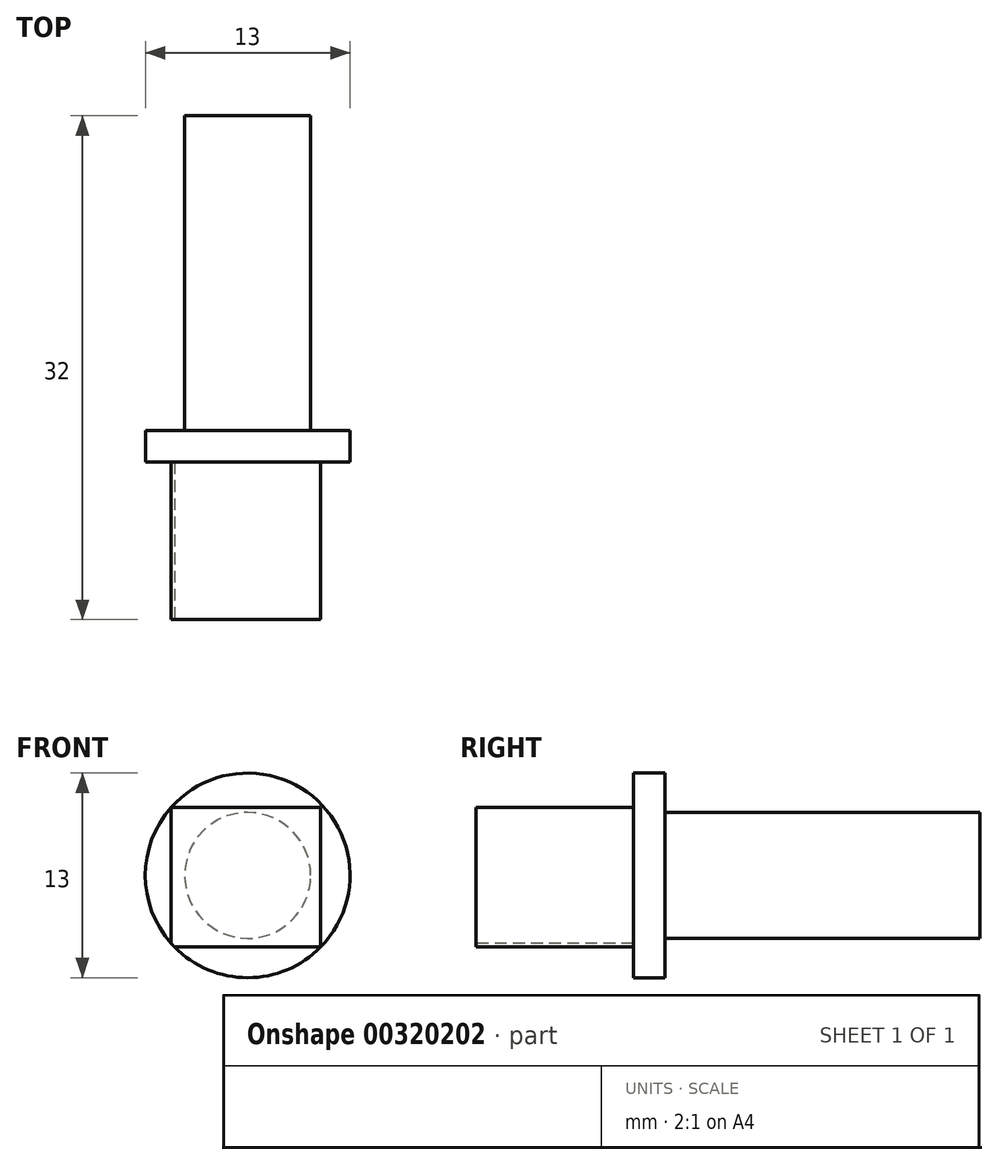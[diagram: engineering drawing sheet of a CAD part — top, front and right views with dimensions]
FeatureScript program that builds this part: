
annotation { "Feature Type Name" : "Feature", "Feature Type Description" : "" }
export const myFeature = defineFeature(function(context is Context, id is Id, definition is map)
    precondition{}
    {
        {
            var Q0;
            Q0=qCreatedBy(makeId("Front.planeOp"),FACE);
            var sketch = newSketch(context, id + "F0", { "sketchPlane" : qUnion([Q0])});
            skCircle(sketch, "E0", {"center": v(0, 0) * mm, "radius": 6.5 * mm});
            skLineSegment(sketch, "E1", {"start": v(-4.44, -4.75) * mm, "end": v(4.44, -4.75) * mm});
            skLineSegment(sketch, "E2", {"start": v(4.44, -4.75) * mm, "end": v(4.44, 4.75) * mm});
            skLineSegment(sketch, "E3", {"start": v(4.44, 4.75) * mm, "end": v(-4.44, 4.75) * mm});
            skLineSegment(sketch, "E4", {"start": v(-4.44, 4.75) * mm, "end": v(-4.44, -4.75) * mm});
            skPoint(sketch, "E5.startSnap0", {"position": v(4.44, 0) * mm});
            skCircle(sketch, "E6", {"center": v(0, 0) * mm, "radius": 4 * mm});
            skSolve(sketch);
        }
        {
            var Q0;
            Q0=makeQuery(id+"F0.imprint","IMPRINT",FACE,{"disambiguationData":[TD([[makeQuery(id+"F0.imprint","IMPRINT",EDGE,{"derivedFrom":sQuery(id+"F0.wireOp",EDGE,"E6")}),1.0]])]});
            extrude(context, id + "F1", {"entities" : qUnion([Q0]), "oppositeDirection" : true, "depth" : 22 * mm});
        }
        {
            var Q0;
            Q0 = qSketchRegion(id + "F0", true);
            extrude(context, id + "F2", {"entities" : qUnion([Q0]), "operationType" : NewBodyOperationType.ADD, "oppositeDirection" : true, "depth" : 2 * mm});
        }
        {
            var Q0;
            {var subQ0=sQuery(id+"F0.wireOp",EDGE,"E6");Q0=makeQuery(id+"F2.boolean.opBoolean","MERGE",FACE,{"derivedFrom":[makeQuery(id+"F1.opExtrude","CAP_FACE",FACE,{"disambiguationData":[OSD([subQ0])],"isStart":true}),makeQuery(id+"F2.opExtrude","CAP_FACE",FACE,{"disambiguationData":[OSD([sQuery(id+"F0.wireOp",EDGE,"E0"),subQ0])],"isStart":true})]});}
            extrude(context, id + "F3", {"entities" : qUnion([Q0]), "operationType" : NewBodyOperationType.ADD, "depth" : 10 * mm});
        }
        {
            var Q0;
            Q0=makeQuery(id+"F3.opExtrude","CAP_FACE",FACE,{"disambiguationData":[OSD([sQuery(id+"F0.wireOp",EDGE,"E0"),sQuery(id+"F0.wireOp",EDGE,"E6")])],"isStart":false});
            var sketch = newSketch(context, id + "F4", { "sketchPlane" : qUnion([Q0])});
            skLineSegment(sketch, "E7.bottom", {"start": v(-4.86, 4.32) * mm, "end": v(4.64, 4.32) * mm});
            skLineSegment(sketch, "E7.top", {"start": v(-4.86, -4.55) * mm, "end": v(4.64, -4.55) * mm});
            skLineSegment(sketch, "E7.left", {"start": v(-4.86, 4.32) * mm, "end": v(-4.86, -4.55) * mm});
            skLineSegment(sketch, "E7.right", {"start": v(4.64, 4.32) * mm, "end": v(4.64, -4.55) * mm});
            skSolve(sketch);
        }
        {
            var Q0;
            {var subQ0=sQuery(id+"F4.wireOp",EDGE,"E7.bottom");Q0=makeQuery(id+"F4.imprint","IMPRINT",FACE,{"disambiguationData":[TD([[makeQuery(id+"F4.imprint","IMPRINT",EDGE,{"derivedFrom":subQ0}),1.0]])]});}
            var Q1;
            {var subQ0=sQuery(id+"F4.wireOp",EDGE,"E7.top");var subQ1=makeQuery(id+"F3.opExtrude","CAP_EDGE",EDGE,{"disambiguationData":[OSD([sQuery(id+"F0.wireOp",EDGE,"E0")])],"isStart":false});var subQ3=makeQuery(id+"F4.imprint","INTERSECT",VERTEX,{"derivedFrom":[subQ1,subQ0]});Q1=makeQuery(id+"F4.imprint","IMPRINT",FACE,{"disambiguationData":[TD([[makeQuery(id+"F4.imprint","IMPRINT",EDGE,{"disambiguationData":[TD([[subQ3,-1.0]])],"derivedFrom":subQ0}),-1.0]])]});}
            var Q2;
            {var subQ0=sQuery(id+"F4.wireOp",EDGE,"E7.left");var subQ1=makeQuery(id+"F3.opExtrude","CAP_EDGE",EDGE,{"disambiguationData":[OSD([sQuery(id+"F0.wireOp",EDGE,"E0")])],"isStart":false});var subQ3=makeQuery(id+"F4.imprint","INTERSECT",VERTEX,{"derivedFrom":[subQ1,subQ0]});Q2=makeQuery(id+"F4.imprint","IMPRINT",FACE,{"disambiguationData":[TD([[makeQuery(id+"F4.imprint","IMPRINT",EDGE,{"disambiguationData":[TD([[subQ3,1.0]])],"derivedFrom":subQ0}),-1.0]])]});}
            extrude(context, id + "F5", {"entities" : qUnion([Q0, Q1, Q2]), "operationType" : NewBodyOperationType.REMOVE, "oppositeDirection" : true, "depth" : 10 * mm});
        }
    });
